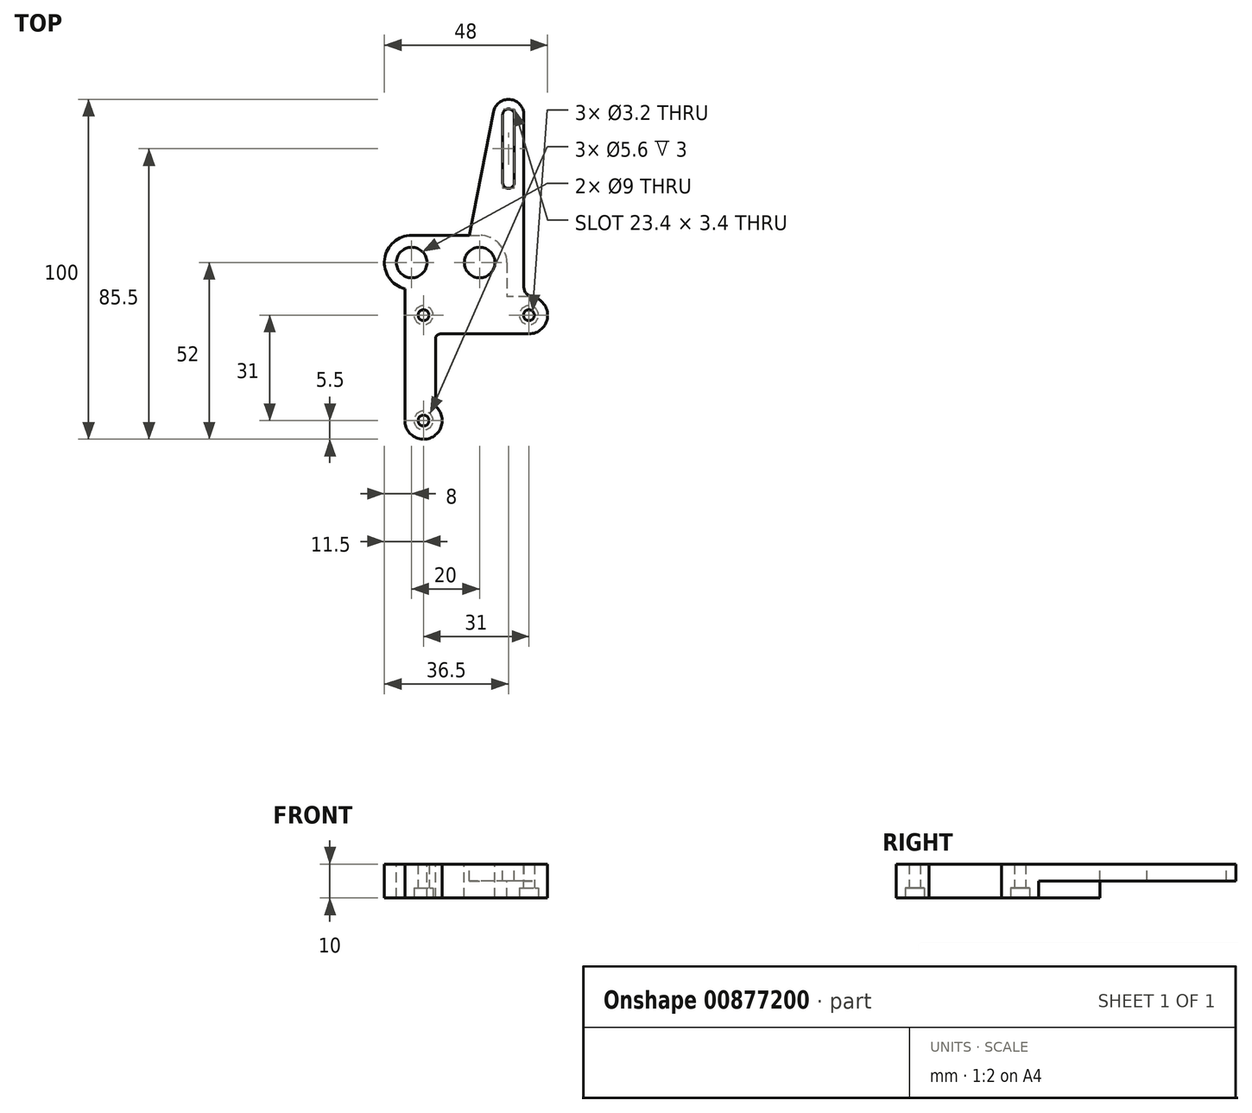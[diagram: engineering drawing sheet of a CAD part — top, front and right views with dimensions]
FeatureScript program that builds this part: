
annotation { "Feature Type Name" : "Feature", "Feature Type Description" : "" }
export const myFeature = defineFeature(function(context is Context, id is Id, definition is map)
    precondition{}
    {
        {
            var Q0;
            Q0=qCreatedBy(makeId("Top.planeOp"),FACE);
            var sketch = newSketch(context, id + "F0", { "sketchPlane" : qUnion([Q0])});
            skCircle(sketch, "E0", {"center": v(-10, 0) * mm, "radius": 4.5 * mm});
            skCircle(sketch, "E1", {"center": v(10, 0) * mm, "radius": 4.5 * mm});
            skCircle(sketch, "E2", {"center": v(-10, 0) * mm, "radius": 8 * mm});
            skCircle(sketch, "E3", {"center": v(10, 0) * mm, "radius": 8 * mm});
            skLineSegment(sketch, "E4", {"start": v(-10, 8) * mm, "end": v(10, 8) * mm});
            skCircle(sketch, "E5", {"center": v(-6.5, -15.5) * mm, "radius": 5.5 * mm});
            skCircle(sketch, "E6", {"center": v(24.5, -15.5) * mm, "radius": 5.5 * mm});
            skCircle(sketch, "E7", {"center": v(-6.5, -46.5) * mm, "radius": 5.5 * mm});
            skLineSegment(sketch, "E8", {"start": v(-12, -46.5) * mm, "end": v(-12, -15.5) * mm});
            skLineSegment(sketch, "E9", {"start": v(-12, -15.5) * mm, "end": v(-12, -7.75) * mm});
            skLineSegment(sketch, "E10", {"start": v(-3, -42.26) * mm, "end": v(-3, -19.74) * mm});
            skLineSegment(sketch, "E11", {"start": v(18, 0) * mm, "end": v(18, -21) * mm});
            skLineSegment(sketch, "E12", {"start": v(24.5, -10) * mm, "end": v(18, -10) * mm});
            skLineSegment(sketch, "E13", {"start": v(24.5, -21) * mm, "end": v(-6.5, -21) * mm});
            skLineSegment(sketch, "E14", {"start": v(23, -10) * mm, "end": v(23, 43.5) * mm});
            skCircle(sketch, "E15", {"center": v(18.5, 43.5) * mm, "radius": 4.5 * mm});
            skLineSegment(sketch, "E16", {"start": v(14.08, 44.36) * mm, "end": v(7, 8) * mm});
            skCircle(sketch, "E17", {"center": v(18.5, 43.5) * mm, "radius": 1.7 * mm});
            skCircle(sketch, "E18", {"center": v(18.5, 23.5) * mm, "radius": 1.7 * mm});
            skLineSegment(sketch, "E19", {"start": v(16.8, 43.5) * mm, "end": v(16.8, 23.5) * mm});
            skLineSegment(sketch, "E20", {"start": v(20.2, 23.5) * mm, "end": v(20.2, 43.5) * mm});
            skSolve(sketch);
        }
        {
            var Q0;
            Q0=qSketchRegion(id+"F0",true);
            var Q1;
            Q1=makeQuery(id+"F0.imprint","IMPRINT",FACE,{"disambiguationData":[TD([[makeQuery(id+"F0.imprint","IMPRINT",EDGE,{"derivedFrom":sQuery(id+"F0.wireOp",EDGE,"0YY4Y7gv-uuNl-tZYm-uvUL-SGIuycmOQimD")}),-1.0]])]});
            var Q2;
            Q2=makeQuery(id+"F0.imprint","IMPRINT",FACE,{"disambiguationData":[TD([[makeQuery(id+"F0.imprint","IMPRINT",EDGE,{"derivedFrom":sQuery(id+"F0.wireOp",EDGE,"mvbghYz6-oLRB-HFOf-AIsI-usYbwoFAbG66")}),-1.0]])]});
            var Q3;
            Q3=makeQuery(id+"F0.imprint","IMPRINT",FACE,{"disambiguationData":[TD([[makeQuery(id+"F0.imprint","IMPRINT",EDGE,{"derivedFrom":sQuery(id+"F0.wireOp",EDGE,"c8FfxmZV-T8WW-zFBv-zk3T-xs9llZKVaEBg")}),-1.0]])]});
            var Q4;
            Q4=makeQuery(id+"F0.imprint","IMPRINT",FACE,{"disambiguationData":[TD([[makeQuery(id+"F0.imprint","IMPRINT",EDGE,{"derivedFrom":sQuery(id+"F0.wireOp",EDGE,"E1")}),-1.0]])]});
            extrude(context, id + "F1", {"entities" : qUnion([Q0, Q1, Q2, Q3, Q4]), "oppositeDirection" : true, "depth" : 5 * mm});
        }
        {
            var Q0;
            {var subQ0=sQuery(id+"F0.wireOp",EDGE,"E6");var subQ1=makeQuery(id+"F0.imprint","INTERSECT",VERTEX,{"derivedFrom":[subQ0,sQuery(id+"F0.wireOp",EDGE,"E12")]});Q0=makeQuery(id+"F0.imprint","IMPRINT",FACE,{"disambiguationData":[TD([[makeQuery(id+"F0.imprint","IMPRINT",EDGE,{"disambiguationData":[TD([[subQ1,-1.0]])],"derivedFrom":subQ0}),1.0]])]});}
            var Q1;
            {var subQ0=sQuery(id+"F0.wireOp",EDGE,"E7");var subQ1=makeQuery(id+"F0.imprint","INTERSECT",VERTEX,{"derivedFrom":[subQ0,sQuery(id+"F0.wireOp",EDGE,"E8")]});Q1=makeQuery(id+"F0.imprint","IMPRINT",FACE,{"disambiguationData":[TD([[makeQuery(id+"F0.imprint","IMPRINT",EDGE,{"disambiguationData":[TD([[subQ1,1.0]])],"derivedFrom":subQ0}),1.0]])]});}
            var Q2;
            Q2=makeQuery(id+"F0.imprint","IMPRINT",FACE,{"disambiguationData":[TD([[makeQuery(id+"F0.imprint","IMPRINT",EDGE,{"derivedFrom":sQuery(id+"F0.wireOp",EDGE,"E0")}),-1.0]])]});
            var Q3;
            {var subQ0=sQuery(id+"F0.wireOp",EDGE,"E5");var subQ3=makeQuery(id+"F0.imprint","INTERSECT",VERTEX,{"derivedFrom":[subQ0,sQuery(id+"F0.wireOp",EDGE,"E10")]});Q3=makeQuery(id+"F0.imprint","IMPRINT",FACE,{"disambiguationData":[TD([[makeQuery(id+"F0.imprint","IMPRINT",EDGE,{"disambiguationData":[TD([[subQ3,1.0]])],"derivedFrom":subQ0}),1.0]])]});}
            var Q4;
            {var subQ5=sQuery(id+"F0.wireOp",EDGE,"E8");Q4=makeQuery(id+"F0.imprint","IMPRINT",FACE,{"disambiguationData":[TD([[makeQuery(id+"F0.imprint","IMPRINT",EDGE,{"derivedFrom":subQ5}),-1.0]])]});}
            var Q5;
            {var subQ0=sQuery(id+"F0.wireOp",EDGE,"E10");var subQ1=sQuery(id+"F0.wireOp",EDGE,"E5");var subQ2=makeQuery(id+"F0.imprint","INTERSECT",VERTEX,{"derivedFrom":[subQ1,subQ0]});Q5=makeQuery(id+"F0.imprint","IMPRINT",FACE,{"disambiguationData":[TD([[makeQuery(id+"F0.imprint","IMPRINT",EDGE,{"disambiguationData":[TD([[subQ2,1.0]])],"derivedFrom":subQ1}),-1.0]])]});}
            var Q6;
            {var subQ0=sQuery(id+"F0.wireOp",EDGE,"E12");var subQ4=sQuery(id+"F0.wireOp",EDGE,"E6");var subQ5=makeQuery(id+"F0.imprint","INTERSECT",VERTEX,{"derivedFrom":[subQ4,subQ0]});Q6=makeQuery(id+"F0.imprint","IMPRINT",FACE,{"disambiguationData":[TD([[makeQuery(id+"F0.imprint","IMPRINT",EDGE,{"disambiguationData":[TD([[subQ5,-1.0]])],"derivedFrom":subQ4}),-1.0]])]});}
            var Q7;
            {var subQ13=sQuery(id+"F0.wireOp",EDGE,"E9");Q7=makeQuery(id+"F0.imprint","IMPRINT",FACE,{"disambiguationData":[TD([[makeQuery(id+"F0.imprint","IMPRINT",EDGE,{"derivedFrom":subQ13}),-1.0]])]});}
            var Q8;
            {var subQ0=sQuery(id+"F0.wireOp",EDGE,"E6");var subQ1=makeQuery(id+"F0.imprint","INTERSECT",VERTEX,{"derivedFrom":[subQ0,sQuery(id+"F0.wireOp",EDGE,"E12")]});Q8=makeQuery(id+"F0.imprint","IMPRINT",FACE,{"disambiguationData":[TD([[makeQuery(id+"F0.imprint","IMPRINT",EDGE,{"disambiguationData":[TD([[subQ1,-1.0]])],"derivedFrom":subQ0}),1.0]])]});}
            var Q9;
            {var subQ0=sQuery(id+"F0.wireOp",EDGE,"E7");var subQ1=makeQuery(id+"F0.imprint","INTERSECT",VERTEX,{"derivedFrom":[subQ0,sQuery(id+"F0.wireOp",EDGE,"E8")]});Q9=makeQuery(id+"F0.imprint","IMPRINT",FACE,{"disambiguationData":[TD([[makeQuery(id+"F0.imprint","IMPRINT",EDGE,{"disambiguationData":[TD([[subQ1,1.0]])],"derivedFrom":subQ0}),1.0]])]});}
            var Q10;
            Q10=makeQuery(id+"F0.imprint","IMPRINT",FACE,{"disambiguationData":[TD([[makeQuery(id+"F0.imprint","IMPRINT",EDGE,{"derivedFrom":sQuery(id+"F0.wireOp",EDGE,"E0")}),-1.0]])]});
            var Q11;
            {var subQ0=sQuery(id+"F0.wireOp",EDGE,"E5");var subQ3=makeQuery(id+"F0.imprint","INTERSECT",VERTEX,{"derivedFrom":[subQ0,sQuery(id+"F0.wireOp",EDGE,"E10")]});Q11=makeQuery(id+"F0.imprint","IMPRINT",FACE,{"disambiguationData":[TD([[makeQuery(id+"F0.imprint","IMPRINT",EDGE,{"disambiguationData":[TD([[subQ3,1.0]])],"derivedFrom":subQ0}),1.0]])]});}
            var Q12;
            {var subQ5=sQuery(id+"F0.wireOp",EDGE,"E8");Q12=makeQuery(id+"F0.imprint","IMPRINT",FACE,{"disambiguationData":[TD([[makeQuery(id+"F0.imprint","IMPRINT",EDGE,{"derivedFrom":subQ5}),-1.0]])]});}
            var Q13;
            {var subQ0=sQuery(id+"F0.wireOp",EDGE,"E10");var subQ1=sQuery(id+"F0.wireOp",EDGE,"E5");var subQ2=makeQuery(id+"F0.imprint","INTERSECT",VERTEX,{"derivedFrom":[subQ1,subQ0]});Q13=makeQuery(id+"F0.imprint","IMPRINT",FACE,{"disambiguationData":[TD([[makeQuery(id+"F0.imprint","IMPRINT",EDGE,{"disambiguationData":[TD([[subQ2,1.0]])],"derivedFrom":subQ1}),-1.0]])]});}
            var Q14;
            {var subQ0=sQuery(id+"F0.wireOp",EDGE,"E12");var subQ4=sQuery(id+"F0.wireOp",EDGE,"E6");var subQ5=makeQuery(id+"F0.imprint","INTERSECT",VERTEX,{"derivedFrom":[subQ4,subQ0]});Q14=makeQuery(id+"F0.imprint","IMPRINT",FACE,{"disambiguationData":[TD([[makeQuery(id+"F0.imprint","IMPRINT",EDGE,{"disambiguationData":[TD([[subQ5,-1.0]])],"derivedFrom":subQ4}),-1.0]])]});}
            var Q15;
            {var subQ13=sQuery(id+"F0.wireOp",EDGE,"E9");Q15=makeQuery(id+"F0.imprint","IMPRINT",FACE,{"disambiguationData":[TD([[makeQuery(id+"F0.imprint","IMPRINT",EDGE,{"derivedFrom":subQ13}),-1.0]])]});}
            var Q16;
            Q16=makeQuery(id+"F0.imprint","IMPRINT",FACE,{"disambiguationData":[TD([[makeQuery(id+"F0.imprint","IMPRINT",EDGE,{"derivedFrom":sQuery(id+"F0.wireOp",EDGE,"E1")}),-1.0]])]});
            extrude(context, id + "F2", {"entities" : qUnion([Q0, Q1, Q2, Q3, Q4, Q5, Q6, Q7, Q8, Q9, Q10, Q11, Q12, Q13, Q14, Q15, Q16]), "operationType" : NewBodyOperationType.ADD, "oppositeDirection" : true, "depth" : 10 * mm});
        }
        {
            var Q0;
            Q0=makeQuery(id+"F2.opExtrude","CAP_FACE",FACE,{"disambiguationData":[OSD([sQuery(id+"F0.wireOp",EDGE,"E0"),sQuery(id+"F0.wireOp",EDGE,"E1"),sQuery(id+"F0.wireOp",EDGE,"E2"),sQuery(id+"F0.wireOp",EDGE,"E3"),sQuery(id+"F0.wireOp",EDGE,"E4"),sQuery(id+"F0.wireOp",EDGE,"E6"),sQuery(id+"F0.wireOp",EDGE,"E7"),sQuery(id+"F0.wireOp",EDGE,"E8"),sQuery(id+"F0.wireOp",EDGE,"E9"),sQuery(id+"F0.wireOp",EDGE,"E10"),sQuery(id+"F0.wireOp",EDGE,"E11"),sQuery(id+"F0.wireOp",EDGE,"E12"),sQuery(id+"F0.wireOp",EDGE,"E13")])],"isStart":false});
            var sketch = newSketch(context, id + "F3", { "sketchPlane" : qUnion([Q0])});
            skPoint(sketch, "E21.0", {"position": v(24.5, 15.5) * mm});
            skPoint(sketch, "E22.0", {"position": v(-6.5, 15.5) * mm});
            skPoint(sketch, "E23.0", {"position": v(-6.5, 46.5) * mm});
            skSolve(sketch);
        }
        {
            var Q0;
            Q0=sQuery(id+"F3.wireOp",VERTEX,"E23.0");
            var Q1;
            Q1=sQuery(id+"F3.wireOp",VERTEX,"E22.0");
            var Q2;
            Q2=sQuery(id+"F3.wireOp",VERTEX,"E21.0");
            var Q3;
            Q3=makeQuery(id+"F1.opExtrude","SWEPT_BODY",BODY,{"disambiguationData":[OSD([sQuery(id+"F0.wireOp",EDGE,"E0"),sQuery(id+"F0.wireOp",EDGE,"E1"),sQuery(id+"F0.wireOp",EDGE,"E2"),sQuery(id+"F0.wireOp",EDGE,"E4"),sQuery(id+"F0.wireOp",EDGE,"E6"),sQuery(id+"F0.wireOp",EDGE,"E7"),sQuery(id+"F0.wireOp",EDGE,"E8"),sQuery(id+"F0.wireOp",EDGE,"E9"),sQuery(id+"F0.wireOp",EDGE,"E10"),sQuery(id+"F0.wireOp",EDGE,"E12"),sQuery(id+"F0.wireOp",EDGE,"E13"),sQuery(id+"F0.wireOp",EDGE,"E14"),sQuery(id+"F0.wireOp",EDGE,"E15"),sQuery(id+"F0.wireOp",EDGE,"E16"),sQuery(id+"F0.wireOp",EDGE,"E17"),sQuery(id+"F0.wireOp",EDGE,"E18"),sQuery(id+"F0.wireOp",EDGE,"E19"),sQuery(id+"F0.wireOp",EDGE,"E20")])]});
            hole(context, id + "F4", {"style" : HoleStyle.C_BORE, "endStyle" : HoleEndStyle.THROUGH, "holeDiameter" : 3.2 * mm, "cBoreDiameter" : 5.6 * mm, "cBoreDepth" : 3 * mm, "tappedDepth" : 12 * mm, "tapClearance" : 3, "locations" : qUnion([Q0, Q1, Q2]), "scope" : qUnion([Q3])});
        }
        {
            var Q0;
            Q0=makeQuery(id+"F1.opExtrude","SWEPT_EDGE",EDGE,{"disambiguationData":[OSD([sQuery(id+"F0.wireOp",EDGE,"E12"),sQuery(id+"F0.wireOp",EDGE,"E14")])]});
            fillet(context, id + "F5", {"entities" : qUnion([Q0]), "radius" : 3 * mm, "tangentPropagation" : true, "allowEdgeOverflow" : false});
        }
        {
            var Q0;
            {var subQ0=sQuery(id+"F0.wireOp",EDGE,"E13");var subQ1=sQuery(id+"F0.wireOp",EDGE,"E10");Q0=makeQuery(id+"F2.boolean.opBoolean","MERGE",EDGE,{"derivedFrom":[makeQuery(id+"F1.opExtrude","SWEPT_EDGE",EDGE,{"disambiguationData":[OSD([subQ1,subQ0])]}),makeQuery(id+"F2.opExtrude","SWEPT_EDGE",EDGE,{"disambiguationData":[OSD([subQ1,subQ0])]})]});}
            fillet(context, id + "F6", {"entities" : qUnion([Q0]), "radius" : 1.5 * mm, "tangentPropagation" : true, "allowEdgeOverflow" : false});
        }
    });
